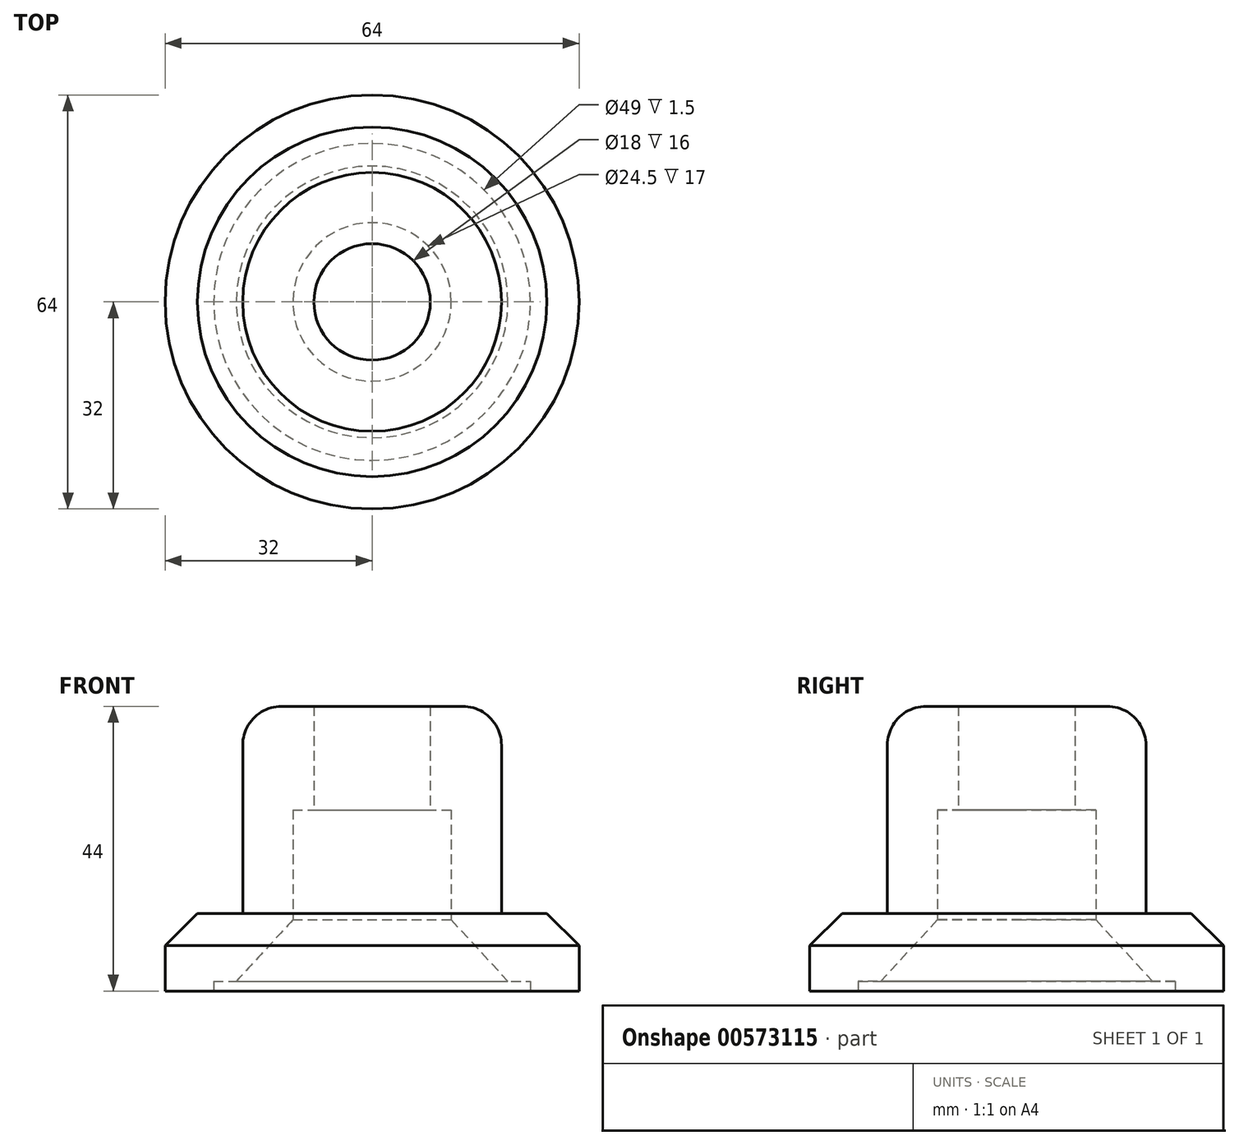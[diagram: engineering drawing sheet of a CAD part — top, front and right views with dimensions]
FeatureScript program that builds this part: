
annotation { "Feature Type Name" : "Feature", "Feature Type Description" : "" }
export const myFeature = defineFeature(function(context is Context, id is Id, definition is map)
    precondition{}
    {
        {
            var Q0;
            Q0=qCreatedBy(makeId("Right.planeOp"),FACE);
            var sketch = newSketch(context, id + "F0", { "sketchPlane" : qUnion([Q0])});
            skLineSegment(sketch, "E0", {"start": v(24.5, 0) * mm, "end": v(32, 0) * mm});
            skLineSegment(sketch, "E1", {"start": v(32, 7) * mm, "end": v(32, 0) * mm});
            skLineSegment(sketch, "E2", {"start": v(32, 7) * mm, "end": v(27, 12) * mm});
            skLineSegment(sketch, "E3", {"start": v(27, 12) * mm, "end": v(20, 12) * mm});
            skLineSegment(sketch, "E4", {"start": v(24.5, 0) * mm, "end": v(24.5, 1.5) * mm});
            skLineSegment(sketch, "E5", {"start": v(24.5, 1.5) * mm, "end": v(21, 1.5) * mm});
            skLineSegment(sketch, "E6", {"start": v(21, 1.5) * mm, "end": v(12.25, 11) * mm});
            skLineSegment(sketch, "E7", {"start": v(12.25, 11) * mm, "end": v(12.25, 28) * mm});
            skLineSegment(sketch, "E8", {"start": v(12.25, 28) * mm, "end": v(9, 28) * mm});
            skLineSegment(sketch, "E9", {"start": v(9, 28) * mm, "end": v(9, 44) * mm});
            skLineSegment(sketch, "E10", {"start": v(0, 0) * mm, "end": v(0, 39.34) * mm, "construction": true});
            skLineSegment(sketch, "E11", {"start": v(9, 44) * mm, "end": v(14, 44) * mm});
            skPoint(sketch, "E12", {"position": v(20, 44) * mm});
            skLineSegment(sketch, "E13", {"start": v(20, 12) * mm, "end": v(20, 38) * mm});
            skPoint(sketch, "E14", {"position": v(20, 38) * mm});
            skArc(sketch, "E15", {"start": v(20, 38) * mm, "mid": v(18.24, 42.24) * mm, "end": v(14, 44) * mm});
            skSolve(sketch);
        }
        {
            var Q0;
            Q0=makeQuery(id+"F0.imprint","IMPRINT",FACE,{"disambiguationData":[TD([[makeQuery(id+"F0.imprint","IMPRINT",EDGE,{"derivedFrom":sQuery(id+"F0.wireOp",EDGE,"E0")}),1.0]])]});
            var Q1;
            Q1=sQuery(id+"F0.wireOp",EDGE,"E10");
            revolve(context, id + "F1", {"entities" : qUnion([Q0]), "axis" : qUnion([Q1]), "revolveType" : RevolveType.FULL});
        }
    });
